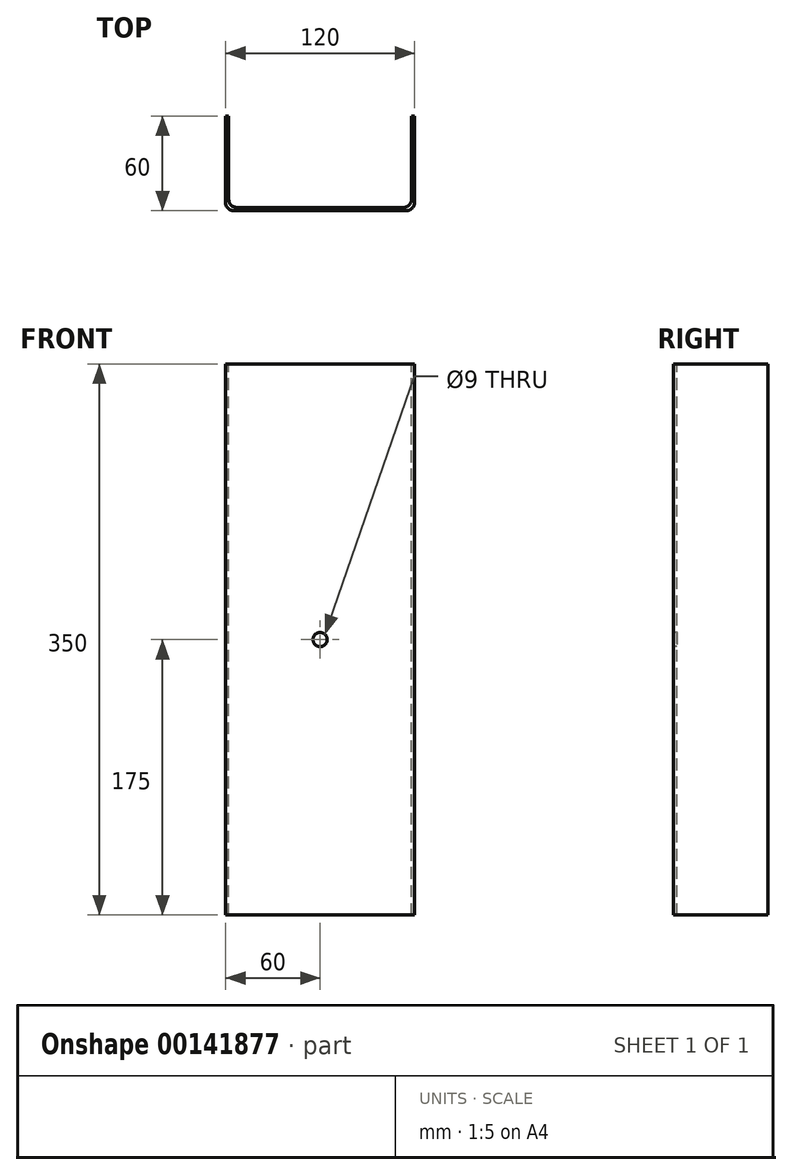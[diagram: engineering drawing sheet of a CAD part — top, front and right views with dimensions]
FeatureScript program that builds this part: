
annotation { "Feature Type Name" : "Feature", "Feature Type Description" : "" }
export const myFeature = defineFeature(function(context is Context, id is Id, definition is map)
    precondition{}
    {
        {
            var Q0;
            Q0=qCreatedBy(makeId("Top.planeOp"),FACE);
            var sketch = newSketch(context, id + "F0", { "sketchPlane" : qUnion([Q0])});
            skLineSegment(sketch, "E0.bottom", {"start": v(60, -30) * mm, "end": v(-60, -30) * mm});
            skLineSegment(sketch, "E0.top", {"start": v(60, 30) * mm, "end": v(-60, 30) * mm});
            skLineSegment(sketch, "E0.left", {"start": v(60, -30) * mm, "end": v(60, 30) * mm});
            skLineSegment(sketch, "E0.right", {"start": v(-60, -30) * mm, "end": v(-60, 30) * mm});
            skPoint(sketch, "E0.middle", {"position": v(0, 0) * mm});
            skSolve(sketch);
        }
        {
            var Q0;
            Q0=makeQuery(id+"F0.imprint","IMPRINT",FACE,{"disambiguationData":[TD([[makeQuery(id+"F0.imprint","IMPRINT",EDGE,{"derivedFrom":sQuery(id+"F0.wireOp",EDGE,"E0.bottom")}),-1.0]])]});
            extrude(context, id + "F1", {"entities" : qUnion([Q0]), "oppositeDirection" : true, "depth" : 350 * mm, "symmetric" : true});
        }
        {
            var Q0;
            Q0=makeQuery(id+"F1.opExtrude","SWEPT_FACE",FACE,{"disambiguationData":[OSD([sQuery(id+"F0.wireOp",EDGE,"E0.top")])]});
            var Q1;
            Q1=makeQuery(id+"F1.opExtrude","CAP_FACE",FACE,{"disambiguationData":[OSD([sQuery(id+"F0.wireOp",EDGE,"E0.bottom"),sQuery(id+"F0.wireOp",EDGE,"E0.top"),sQuery(id+"F0.wireOp",EDGE,"E0.left"),sQuery(id+"F0.wireOp",EDGE,"E0.right")])],"isStart":true});
            var Q2;
            Q2=makeQuery(id+"F1.opExtrude","CAP_FACE",FACE,{"disambiguationData":[OSD([sQuery(id+"F0.wireOp",EDGE,"E0.bottom"),sQuery(id+"F0.wireOp",EDGE,"E0.top"),sQuery(id+"F0.wireOp",EDGE,"E0.left"),sQuery(id+"F0.wireOp",EDGE,"E0.right")])],"isStart":false});
            shell(context, id + "F2", {"entities" : qUnion([Q0, Q1, Q2]), "thickness" : 2 * mm});
        }
        {
            var Q0;
            Q0=makeQuery(id+"F1.opExtrude","SWEPT_EDGE",EDGE,{"disambiguationData":[OSD([sQuery(id+"F0.wireOp",EDGE,"E0.bottom"),sQuery(id+"F0.wireOp",EDGE,"E0.left")])]});
            var Q1;
            Q1=makeQuery(id+"F2.opShell","OFFSET_EDGE",EDGE,{"disambiguationData":[OSD([sQuery(id+"F0.wireOp",EDGE,"E0.bottom"),sQuery(id+"F0.wireOp",EDGE,"E0.right")])]});
            var Q2;
            Q2=makeQuery(id+"F2.opShell","OFFSET_EDGE",EDGE,{"disambiguationData":[OSD([sQuery(id+"F0.wireOp",EDGE,"E0.bottom"),sQuery(id+"F0.wireOp",EDGE,"E0.left")])]});
            var Q3;
            Q3=makeQuery(id+"F1.opExtrude","SWEPT_EDGE",EDGE,{"disambiguationData":[OSD([sQuery(id+"F0.wireOp",EDGE,"E0.bottom"),sQuery(id+"F0.wireOp",EDGE,"E0.right")])]});
            fillet(context, id + "F3", {"entities" : qUnion([Q0, Q1, Q2, Q3]), "radius" : 5 * mm, "tangentPropagation" : true, "allowEdgeOverflow" : false});
        }
        {
            var Q0;
            Q0=makeQuery(id+"F1.opExtrude","SWEPT_FACE",FACE,{"disambiguationData":[OSD([sQuery(id+"F0.wireOp",EDGE,"E0.bottom")])]});
            var sketch = newSketch(context, id + "F4", { "sketchPlane" : qUnion([Q0])});
            skCircle(sketch, "E1", {"center": v(0, 0) * mm, "radius": 4.5 * mm});
            skSolve(sketch);
        }
        {
            var Q0;
            Q0=makeQuery(id+"F4.imprint","IMPRINT",FACE,{"disambiguationData":[TD([[makeQuery(id+"F4.imprint","IMPRINT",EDGE,{"derivedFrom":sQuery(id+"F4.wireOp",EDGE,"E1")}),1.0]])]});
            extrude(context, id + "F5", {"entities" : qUnion([Q0]), "operationType" : NewBodyOperationType.REMOVE, "endBound" : BoundingType.THROUGH_ALL, "oppositeDirection" : true, "depth" : 25 * mm});
        }
    });
